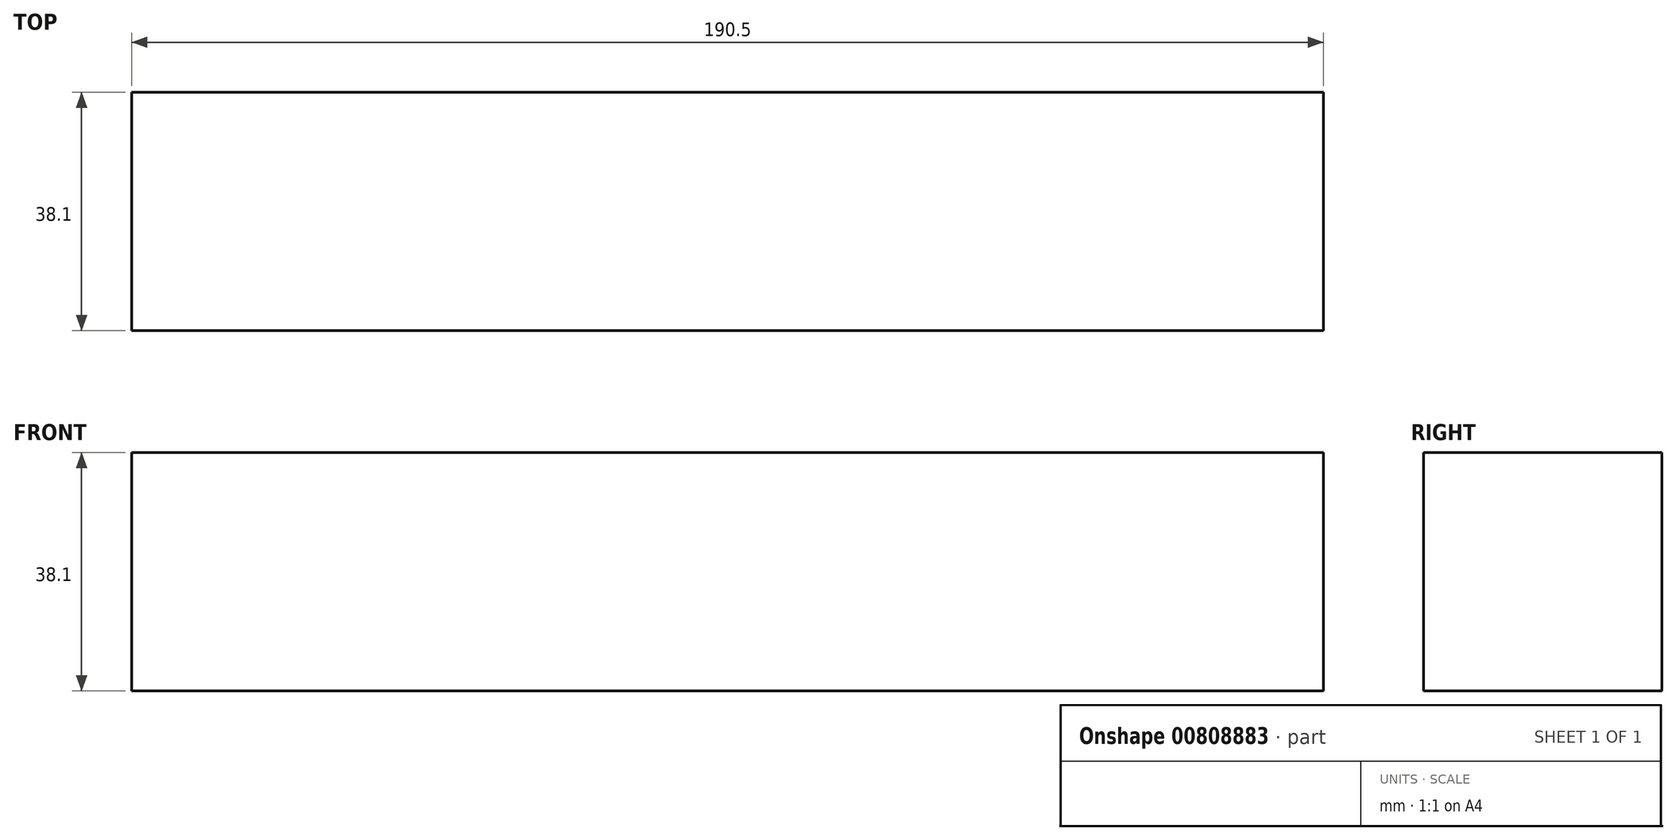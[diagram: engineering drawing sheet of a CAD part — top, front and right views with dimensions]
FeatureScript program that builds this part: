
annotation { "Feature Type Name" : "Feature", "Feature Type Description" : "" }
export const myFeature = defineFeature(function(context is Context, id is Id, definition is map)
    precondition{}
    {
        {
            var Q0;
            Q0=qCreatedBy(makeId("Top.planeOp"),FACE);
            var sketch = newSketch(context, id + "F0", { "sketchPlane" : qUnion([Q0])});
            skLineSegment(sketch, "E0.bottom", {"start": v(-154.48, 23.2) * mm, "end": v(36.02, 23.2) * mm});
            skLineSegment(sketch, "E0.top", {"start": v(-154.48, -14.9) * mm, "end": v(36.02, -14.9) * mm});
            skLineSegment(sketch, "E0.left", {"start": v(-154.48, 23.2) * mm, "end": v(-154.48, -14.9) * mm});
            skLineSegment(sketch, "E0.right", {"start": v(36.02, 23.2) * mm, "end": v(36.02, -14.9) * mm});
            skSolve(sketch);
        }
        {
            var Q0;
            Q0 = qSketchRegion(id + "F0", true);
            extrude(context, id + "F1", {"entities" : qUnion([Q0]), "depth" : 38.1 * mm, "offsetDistance" : 25.4 * mm});
        }
    });
